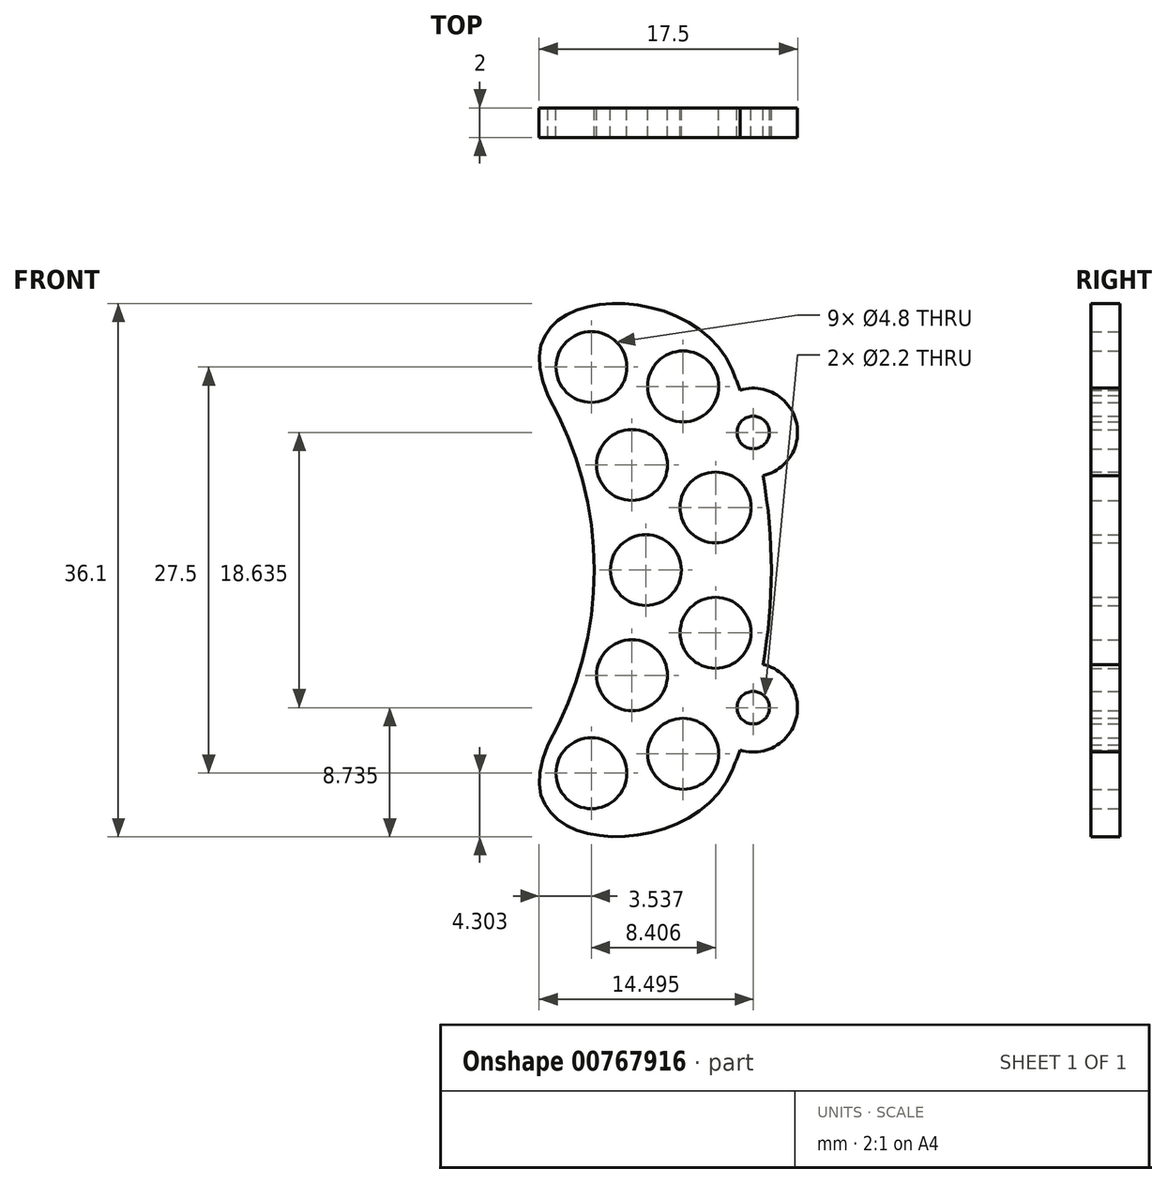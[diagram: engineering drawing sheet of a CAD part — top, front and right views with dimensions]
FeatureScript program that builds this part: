
annotation { "Feature Type Name" : "Feature", "Feature Type Description" : "" }
export const myFeature = defineFeature(function(context is Context, id is Id, definition is map)
    precondition{}
    {
        {
            var Q0;
            Q0=qCreatedBy(makeId("Front.planeOp"),FACE);
            var sketch = newSketch(context, id + "F0", { "sketchPlane" : qUnion([Q0])});
            skPoint(sketch, "E0.center", {"position": v(257.64, -71.7) * mm});
            skArc(sketch, "E1.MirrorCS", {"start": v(278.52, -59.88) * mm, "mid": v(278.92, -60.6) * mm, "end": v(279.29, -61.34) * mm});
            skFitSpline(sketch, "E2.MirrorCS", {"points": [v(290.98, -58.12) * mm, v(278.52, -59.88) * mm], "startDerivative": vector(-7.87, 19.2) * mm, "endDerivative": vector(10.77, -23.32) * mm});
            skArc(sketch, "E3.MirrorCS", {"start": v(290.98, -58.12) * mm, "mid": v(291.26, -58.82) * mm, "end": v(291.52, -59.53) * mm});
            skFitSpline(sketch, "E4.MirrorCS", {"points": [v(290.98, -85.3) * mm, v(278.52, -83.54) * mm], "startDerivative": vector(-7.87, -19.2) * mm, "endDerivative": vector(10.77, 23.32) * mm});
            skArc(sketch, "E5.MirrorCS", {"start": v(279.29, -82.07) * mm, "mid": v(278.92, -82.81) * mm, "end": v(278.52, -83.54) * mm});
            skCircle(sketch, "E6.MirrorC", {"center": v(281.46, -85.46) * mm, "radius": 2.4 * mm});
            skCircle(sketch, "E7.MirrorC", {"center": v(287.67, -84.14) * mm, "radius": 2.4 * mm});
            skCircle(sketch, "E8.MirrorC", {"center": v(284.2, -78.83) * mm, "radius": 2.4 * mm});
            skCircle(sketch, "E9.MirrorC", {"center": v(289.86, -75.95) * mm, "radius": 2.4 * mm});
            skCircle(sketch, "E10.MirrorC", {"center": v(285.14, -71.7) * mm, "radius": 2.4 * mm});
            skCircle(sketch, "E11.MirrorC", {"center": v(289.86, -67.47) * mm, "radius": 2.4 * mm});
            skCircle(sketch, "E12.MirrorC", {"center": v(284.2, -64.59) * mm, "radius": 2.4 * mm});
            skCircle(sketch, "E13.MirrorC", {"center": v(287.67, -59.27) * mm, "radius": 2.4 * mm});
            skCircle(sketch, "E14.MirrorC", {"center": v(281.46, -57.96) * mm, "radius": 2.4 * mm});
            skArc(sketch, "E15", {"start": v(279.29, -82.07) * mm, "mid": v(281.64, -71.7) * mm, "end": v(279.29, -61.34) * mm});
            skCircle(sketch, "E16", {"center": v(292.42, -81.03) * mm, "radius": 1.1 * mm});
            skArc(sketch, "E17", {"start": v(291.52, -83.89) * mm, "mid": v(295.31, -81.8) * mm, "end": v(293.07, -78.1) * mm});
            skArc(sketch, "E18.trimOffspring", {"start": v(291.52, -83.89) * mm, "mid": v(291.26, -84.6) * mm, "end": v(290.98, -85.3) * mm});
            skCircle(sketch, "E19.MirrorC", {"center": v(292.42, -62.4) * mm, "radius": 1.1 * mm});
            skArc(sketch, "E20.MirrorCS", {"start": v(291.52, -59.53) * mm, "mid": v(295.31, -61.61) * mm, "end": v(293.07, -65.32) * mm});
            skArc(sketch, "E21.trimOffspring", {"start": v(293.07, -65.32) * mm, "mid": v(293.64, -71.7) * mm, "end": v(293.07, -78.1) * mm});
            skSolve(sketch);
        }
        {
            var Q0;
            Q0 = qSketchRegion(id + "F0", true);
            extrude(context, id + "F1", {"entities" : qUnion([Q0]), "depth" : 2 * mm, "offsetDistance" : 25 * mm});
        }
    });
